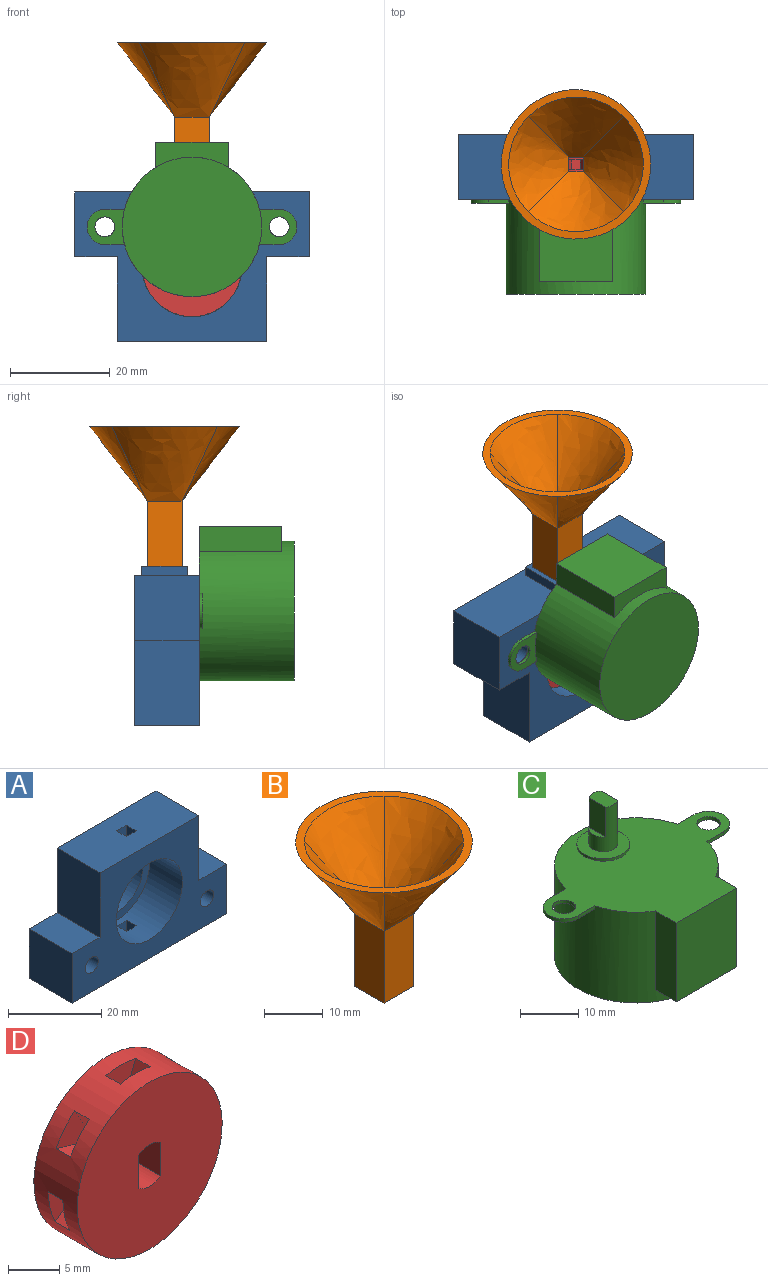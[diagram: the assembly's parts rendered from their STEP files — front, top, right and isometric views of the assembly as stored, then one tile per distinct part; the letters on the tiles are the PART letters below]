
ASSEMBLY  parts=4 mates=4
PART A: 33 faces, bbox 47x13x32 mm
  f0: plane 7.2x7.2mm, normal (0,0,-1), area 42.8mm2, adj f16,f17,f18,f19,f27,f28,f29,f30
  f1: plane 47x13mm, normal (0,0,-1), area 526.4mm2, adj f6,f7,f12,f13,f24,f25,f26,f31
  f2: plane 30x13mm, normal (0,0,1), area 381mm2, adj f4,f9,f12,f13,f20,f21,f22,f23
  f3: cylinder r=10.05mm len=20.1mm, axis (0,1,0), area 613.4mm2, adj f12,f15,f16,f17,f18,f19,f20,f21
  f4: plane 17x13mm, normal (-1,0,0), area 221mm2, adj f2,f5,f12,f13
  f5: plane 13x8.5mm, normal (0,0,1), area 110.5mm2, adj f4,f6,f12,f13
  f6: plane 13x13mm, normal (-1,0,0), area 169mm2, adj f1,f5,f12,f13
  f7: plane 13x13mm, normal (1,0,0), area 169mm2, adj f1,f8,f12,f13
  f8: plane 13x8.5mm, normal (0,0,1), area 110.5mm2, adj f7,f9,f12,f13
  f9: plane 17x13mm, normal (1,0,0), area 221mm2, adj f2,f8,f12,f13
  f10: cylinder r=2mm len=13mm, axis (0,1,0), area 163.4mm2, adj f12,f13
  f11: cylinder r=2mm len=13mm, axis (0,1,0), area 163.4mm2, adj f12,f13
  f12: plane 47x30mm, normal (0,-1,0), area 778.6mm2, adj f1,f2,f3,f4,f5,f6,f7,f8
  f13: plane 47x30mm, normal (0,1,0), area 894.8mm2, adj f1,f2,f4,f5,f6,f7,f8,f9
  f14: cylinder r=8mm len=16mm, axis (0,1,0), area 150.8mm2, adj f13,f15
  f15: plane 20.1x20.1mm, normal (0,-1,0), area 116.2mm2, adj f3,f14
  f16: plane 5.06x3mm, normal (-1,0,0), area 15.2mm2, adj f0,f3,f17,f19
  f17: plane 5.06x3mm, normal (0,1,0), area 15mm2, adj f0,f3,f16,f18
  f18: plane 5.06x3mm, normal (1,0,0), area 15.2mm2, adj f0,f3,f17,f19
  f19: plane 5.06x3mm, normal (0,-1,0), area 15mm2, adj f0,f3,f16,f18
  f20: plane 5.06x3mm, normal (0,-1,0), area 15mm2, adj f2,f3,f21,f23
  f21: plane 5.06x3mm, normal (1,0,0), area 15.2mm2, adj f2,f3,f20,f22
  f22: plane 5.06x3mm, normal (0,1,0), area 15mm2, adj f2,f3,f21,f23
  f23: plane 5.06x3mm, normal (-1,0,0), area 15.2mm2, adj f2,f3,f20,f22
  f24: plane 9.2x2mm, normal (0,-1,0), area 18.4mm2, adj f1,f25,f31,f32
  f25: plane 9.2x2mm, normal (-1,0,0), area 18.4mm2, adj f1,f24,f26,f32
  f26: plane 9.2x2mm, normal (0,1,0), area 18.4mm2, adj f1,f25,f31,f32
  f27: plane 7.2x2mm, normal (1,0,0), area 14.4mm2, adj f0,f28,f30,f32
  f28: plane 7.2x2mm, normal (0,1,0), area 14.4mm2, adj f0,f27,f29,f32
  f29: plane 7.2x2mm, normal (-1,0,0), area 14.4mm2, adj f0,f28,f30,f32
  f30: plane 7.2x2mm, normal (0,-1,0), area 14.4mm2, adj f0,f27,f29,f32
  f31: plane 9.2x2mm, normal (1,0,0), area 18.4mm2, adj f1,f24,f26,f32
  f32: plane 9.2x9.2mm, normal (0,0,-1), area 32.8mm2, adj f24,f25,f26,f27,f28,f29,f30,f31
PART B: 18 faces, bbox 30x30x30 mm
  f0: plane 15x7mm, normal (0,1,0), area 105mm2, adj f1,f3,f4,f10
  f1: plane 15x7mm, normal (-1,0,0), area 105mm2, adj f0,f2,f4,f13
  f2: plane 15x7mm, normal (0,-1,0), area 105mm2, adj f1,f3,f4,f12
  f3: plane 15x7mm, normal (1,0,0), area 105mm2, adj f0,f2,f4,f11
  f4: plane 7x7mm, normal (0,0,-1), area 40mm2, adj f0,f1,f2,f3,f5,f6,f7,f8
  f5: plane 15x3mm, normal (0,1,0), area 45mm2, adj f4,f6,f8,f17
  f6: plane 15x3mm, normal (-1,0,0), area 45mm2, adj f4,f5,f7,f14
  f7: plane 15x3mm, normal (0,-1,0), area 45mm2, adj f4,f6,f8,f15
  f8: plane 15x3mm, normal (1,0,0), area 45mm2, adj f4,f5,f7,f16
  f9: plane 30x30mm, normal (0,0,1), area 134.3mm2, adj f10,f11,f12,f13,f14,f15,f16,f17
  f10: bspline ~21.21x15mm, area 279.8mm2, adj f0,f9,f11,f13
  f11: bspline ~21.21x15mm, area 279.8mm2, adj f3,f9,f10,f12
  f12: bspline ~21.21x15mm, area 279.8mm2, adj f2,f9,f11,f13
  f13: bspline ~21.21x15mm, area 279.8mm2, adj f1,f9,f10,f12
  f14: bspline ~19.09x15mm, area 228.6mm2, adj f6,f9,f15,f17
  f15: bspline ~19.09x15mm, area 228.6mm2, adj f7,f9,f14,f16
  f16: bspline ~19.09x15mm, area 228.6mm2, adj f8,f9,f15,f17
  f17: bspline ~19.09x15mm, area 228.6mm2, adj f5,f9,f14,f16
PART C: 25 faces, bbox 42.1x31x28.8 mm
  f0: cylinder r=14mm len=28mm, axis (0,0,1), area 1407.9mm2, adj f1,f2,f3,f4,f7,f8,f9,f12
  f1: plane 28x28mm, normal (0,0,-1), area 615.8mm2, adj f0
  f2: plane 42.1x31mm, normal (0,0,1), area 671.9mm2, adj f0,f3,f4,f5,f6,f8,f9,f10
  f3: plane 3.96x0.7mm, normal (0,1,0), area 2.8mm2, adj f0,f2,f5,f7
  f4: plane 3.96x0.7mm, normal (0,-1,0), area 2.8mm2, adj f0,f2,f5,f7
  f5: cylinder r=3.55mm len=7.1mm, axis (0,0,1), area 7.8mm2, adj f2,f3,f4,f7
  f6: cylinder r=2mm len=4mm, axis (0,0,1), area 8.8mm2, adj f2,f7
  f7: plane 7.51x7.1mm, normal (0,0,-1), area 33.2mm2, adj f0,f3,f4,f5,f6
  f8: plane 3.96x0.7mm, normal (0,-1,0), area 2.8mm2, adj f0,f2,f10,f12
  f9: plane 3.96x0.7mm, normal (0,1,0), area 2.8mm2, adj f0,f2,f10,f12
  f10: cylinder r=3.55mm len=7.1mm, axis (0,0,1), area 7.8mm2, adj f2,f8,f9,f12
  f11: cylinder r=2mm len=4mm, axis (0,0,1), area 8.8mm2, adj f2,f12
  f12: plane 7.51x7.1mm, normal (0,0,-1), area 33.2mm2, adj f0,f8,f9,f10,f11
  f13: plane 16.5x5.05mm, normal (-1,0,0), area 83.4mm2, adj f0,f2,f14,f16
  f14: plane 16.5x14.6mm, normal (0,-1,0), area 240.9mm2, adj f2,f13,f15,f16
  f15: plane 16.5x5.05mm, normal (1,0,0), area 83.4mm2, adj f0,f2,f14,f16
  f16: plane 14.6x5.05mm, normal (0,0,-1), area 53.5mm2, adj f0,f13,f14,f15
  f17: cylinder r=4.5mm len=9mm, axis (0,0,-1), area 14.1mm2, adj f2,f18
  f18: plane 9x9mm, normal (0,0,1), area 44.8mm2, adj f17,f19
  f19: cylinder r=2.45mm len=9.3mm, axis (0,0,-1), area 86.2mm2, adj f18,f20,f21,f22,f23,f24
  f20: plane 3.95x1mm, normal (0,0,1), area 2.8mm2, adj f19,f23
  f21: plane 3.95x1mm, normal (0,0,1), area 2.8mm2, adj f19,f22
  f22: plane 6.2x3.95mm, normal (1,0,0), area 24.5mm2, adj f19,f21,f24
  f23: plane 6.2x3.95mm, normal (-1,0,0), area 24.5mm2, adj f19,f20,f24
  f24: plane 4.9x2.9mm, normal (0,0,1), area 13.3mm2, adj f19,f22,f23
PART D: 42 faces, bbox 20x6x20 mm
  f0: plane 20x20mm, normal (0,-1,0), area 300.1mm2, adj f2,f38,f39,f40,f41
  f1: plane 20x20mm, normal (0,1,0), area 300.1mm2, adj f2,f38,f39,f40,f41
  f2: cylinder r=10mm len=20mm, axis (0,1,0), area 318.6mm2, adj f0,f1,f3,f4,f5,f6,f8,f9
  f3: plane 4.14x3.25mm, normal (0,-1,0), area 9.4mm2, adj f2,f5,f6,f7
  f4: plane 4.14x3.25mm, normal (0,1,0), area 9.4mm2, adj f2,f5,f6,f7
  f5: plane 3.03x2mm, normal (-0.93,0,0.38), area 6.5mm2, adj f2,f3,f4,f7
  f6: plane 3.04x2mm, normal (0.93,0,0.38), area 6.6mm2, adj f2,f3,f4,f7
  f7: plane 2x1.68mm, normal (-0.01,0,1), area 3.4mm2, adj f3,f4,f5,f6
  f8: plane 4.19x4.16mm, normal (0,-1,0), area 9.4mm2, adj f2,f10,f11,f12
  f9: plane 4.19x4.16mm, normal (0,1,0), area 9.4mm2, adj f2,f10,f11,f12
  f10: plane 2.86x2mm, normal (0.87,0,-0.49), area 6.6mm2, adj f2,f8,f9,f11
  f11: plane 2x1.31mm, normal (0.78,0,0.63), area 3.4mm2, adj f8,f9,f10,f12
  f12: plane 3.13x2mm, normal (-0.28,0,0.96), area 6.5mm2, adj f2,f8,f9,f11
  f13: plane 4.04x3.6mm, normal (0,-1,0), area 9.4mm2, adj f2,f15,f16,f17
  f14: plane 4.04x3.6mm, normal (0,1,0), area 9.4mm2, adj f2,f15,f16,f17
  f15: plane 3.23x2mm, normal (0.16,0,-0.99), area 6.6mm2, adj f2,f13,f14,f16
  f16: plane 2x1.64mm, normal (0.98,0,-0.22), area 3.4mm2, adj f13,f14,f15,f17
  f17: plane 2.68x2mm, normal (0.57,0,0.82), area 6.5mm2, adj f2,f13,f14,f16
  f18: plane 4x3.94mm, normal (0,-1,0), area 9.4mm2, adj f2,f20,f21,f22
  f19: plane 4x3.94mm, normal (0,1,0), area 9.4mm2, adj f2,f20,f21,f22
  f20: plane 2.43x2.2mm, normal (-0.67,0,-0.74), area 6.6mm2, adj f2,f18,f19,f21
  f21: plane 2x1.51mm, normal (0.44,0,-0.9), area 3.4mm2, adj f18,f19,f20,f22
  f22: plane 3.26x2mm, normal (1,0,0.06), area 6.5mm2, adj f2,f18,f19,f21
  f23: plane 3.99x3.94mm, normal (0,-1,0), area 9.4mm2, adj f2,f25,f26,f27
  f24: plane 3.99x3.94mm, normal (0,1,0), area 9.4mm2, adj f2,f25,f26,f27
  f25: plane 3.27x2mm, normal (-1,0,0.06), area 6.6mm2, adj f2,f23,f24,f26
  f26: plane 2x1.52mm, normal (-0.43,0,-0.9), area 3.4mm2, adj f23,f24,f25,f27
  f27: plane 2.42x2.19mm, normal (0.67,0,-0.74), area 6.5mm2, adj f2,f23,f24,f26
  f28: plane 4.04x3.61mm, normal (0,-1,0), area 9.4mm2, adj f2,f30,f31,f32
  f29: plane 4.04x3.61mm, normal (0,1,0), area 9.4mm2, adj f2,f30,f31,f32
  f30: plane 2.68x2mm, normal (-0.57,0,0.82), area 6.6mm2, adj f2,f28,f29,f31
  f31: plane 2x1.63mm, normal (-0.97,0,-0.23), area 3.4mm2, adj f28,f29,f30,f32
  f32: plane 3.22x2mm, normal (-0.16,0,-0.99), area 6.5mm2, adj f2,f28,f29,f31
  f33: plane 4.18x4.17mm, normal (0,-1,0), area 9.4mm2, adj f2,f35,f36,f37
  f34: plane 4.18x4.17mm, normal (0,1,0), area 9.4mm2, adj f2,f35,f36,f37
  f35: plane 3.14x2mm, normal (0.28,0,0.96), area 6.6mm2, adj f2,f33,f34,f36
  f36: plane 2x1.32mm, normal (-0.79,0,0.62), area 3.4mm2, adj f33,f34,f35,f37
  f37: plane 2.85x2mm, normal (-0.87,0,-0.49), area 6.5mm2, adj f2,f33,f34,f36
  f38: cylinder r=2.5mm len=6mm, axis (0,-1,0), area 19.3mm2, adj f0,f1,f39,f41
  f39: plane 6x4mm, normal (1,0,0), area 24mm2, adj f0,f1,f38,f40
  f40: cylinder r=2.5mm len=6mm, axis (0,-1,0), area 19.3mm2, adj f0,f1,f39,f41
  f41: plane 6x4mm, normal (-1,0,0), area 24mm2, adj f0,f1,f38,f40
PLACE A rot(axis=(0,-1,0),180deg) t=(57.94,-27.4,34.77)mm
PLACE B rot(axis=(-0.48,-0.43,0.76),0deg) t=(54.44,-29.9,49.77)mm
PLACE C rot(axis=(-1,0,0),90deg) t=(57.94,-40.4,42.77)mm
PLACE D t=(57.94,-30.4,34.77)mm
MATE fastened B.f4 <-> A.f0  axis (0,0,1) through (57.94,-33.4,49.77)mm
MATE fastened A.f11 <-> C.f6  axis (0,1,0) through (75.44,-40.4,42.77)mm
MATE revolute A.f14 <-> D.f2  axis (0,1,0) through (57.94,-30.4,34.77)mm
MATE fastened A.f10 <-> C.f11  axis (0,1,0) through (40.44,-40.4,42.77)mm
